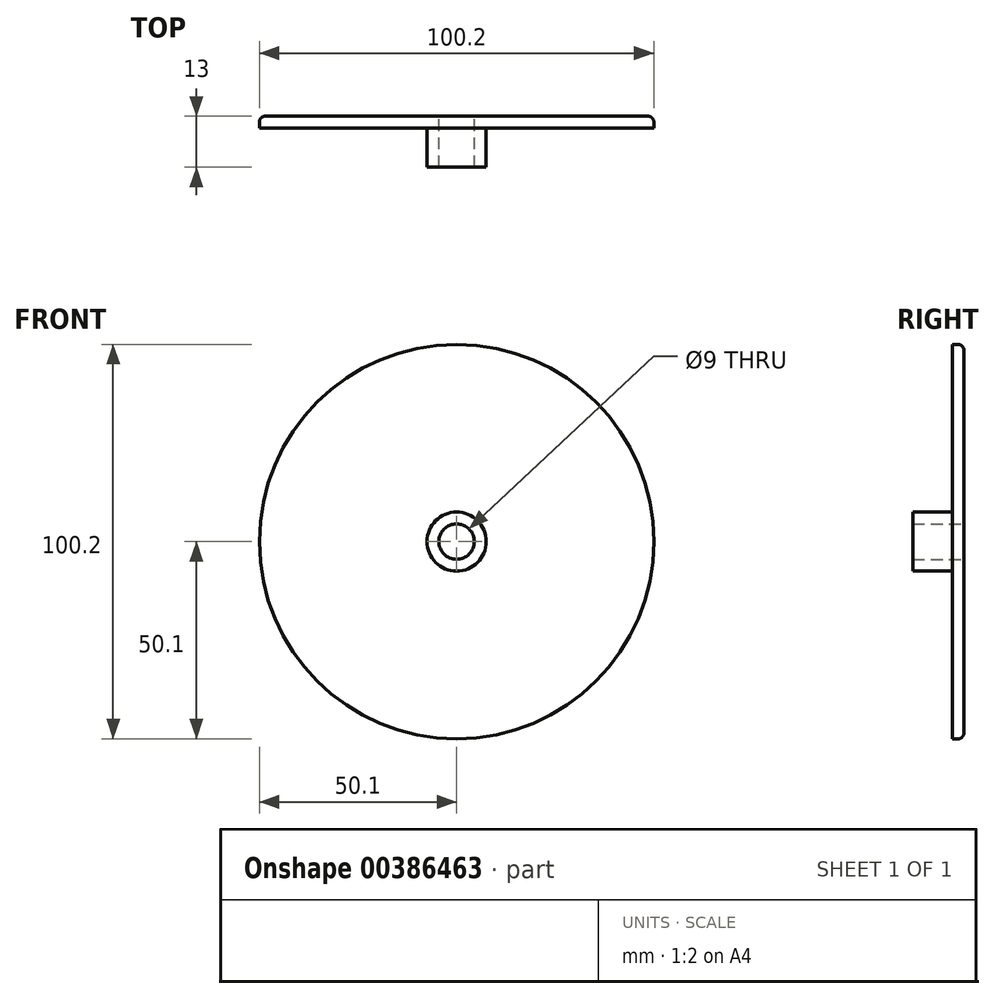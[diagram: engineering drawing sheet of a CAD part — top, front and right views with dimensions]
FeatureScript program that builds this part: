
annotation { "Feature Type Name" : "Feature", "Feature Type Description" : "" }
export const myFeature = defineFeature(function(context is Context, id is Id, definition is map)
    precondition{}
    {
        {
            var Q0;
            Q0=qCreatedBy(makeId("Front.planeOp"),FACE);
            var sketch = newSketch(context, id + "F0", { "sketchPlane" : qUnion([Q0])});
            skCircle(sketch, "E0", {"center": v(0, 0) * mm, "radius": 50.1 * mm});
            skCircle(sketch, "E1", {"center": v(0, 0) * mm, "radius": 4.5 * mm});
            skSolve(sketch);
        }
        {
            var Q0;
            Q0 = qSketchRegion(id + "F0", true);
            extrude(context, id + "F1", {"entities" : qUnion([Q0]), "depth" : 3 * mm});
        }
        {
            var Q0;
            Q0=makeQuery(id+"F1.opExtrude","CAP_FACE",FACE,{"disambiguationData":[OSD([sQuery(id+"F0.wireOp",EDGE,"E0"),sQuery(id+"F0.wireOp",EDGE,"E1")])],"isStart":false});
            var sketch = newSketch(context, id + "F2", { "sketchPlane" : qUnion([Q0])});
            skCircle(sketch, "E2", {"center": v(0, 0) * mm, "radius": 4.5 * mm});
            skCircle(sketch, "E3", {"center": v(0, 0) * mm, "radius": 7.5 * mm});
            skSolve(sketch);
        }
        {
            var Q0;
            Q0 = qSketchRegion(id + "F2", true);
            extrude(context, id + "F3", {"entities" : qUnion([Q0]), "operationType" : NewBodyOperationType.ADD, "depth" : 10 * mm});
        }
        {
            var Q0;
            Q0=makeQuery(id+"F1.opExtrude","CAP_EDGE",EDGE,{"disambiguationData":[OSD([sQuery(id+"F0.wireOp",EDGE,"E0")])],"isStart":true});
            fillet(context, id + "F4", {"entities" : qUnion([Q0]), "radius" : 1.5 * mm, "tangentPropagation" : true, "allowEdgeOverflow" : false});
        }
    });
